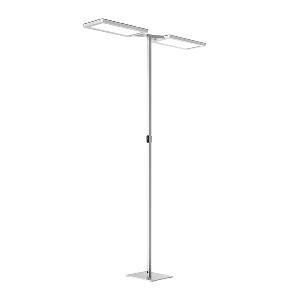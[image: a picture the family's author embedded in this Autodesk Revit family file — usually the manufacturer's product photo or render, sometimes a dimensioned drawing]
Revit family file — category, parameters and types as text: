
# Revit family: yara_doublet_-_yts_2_15000_vtl_r_sr_cee_s0_c_114268000-00808493_cb8c
name_source: partatom
category: Lighting Fixtures
units: mm (PartAtom-declared; Revit-internal decimal feet)

## family parameters
Cut with Voids When Loaded = No
Host = Face
Light Source = No
Part Type = Normal
Room Calculation Point = No
Round Connector Dimension = Use Diameter
Shared = No

## types (1)
- YARA.doubleT - YTS 2/15000/VTL/R/SR/CEE/S0/C (1 x LED, 15000 lm, VTL)
    Apparent Load = 214 VA
    Approval mark = CE
    CIE Flux Codes = 58 87 97 13 100
    Color Rendering = 80-89
    Color Temperature = VTL
    Control Gear = Electronic ballast
    Default Elevation = 1800 mm
    Description = YTS 2/15000/VTL/R/SR/CEE/S0/R|Free-standing luminaire|light source: LED Daylight 2700-6500 K  Energy efficiency category A/A+/A++|work equipment: Electronic ballast DALI|connected load: 220-240 V, 50/60 Hz|Power consumption: approx. 210 W|power factor: approx. 0,966|luminous flux: 30000 lm|luminous efficacy: 142 lm/W|light distribution: Direct/indirect|direct ratio: approx. 13 %|color rendering index (CRI): >= 80|chromaticity tolerance:  3 SDCM|technology: Presence and daylight sensor control (PIR)|operation: Wireless switch|luminaire body|material: Aluminium/plastic|surface: Powder coatet|colour: Silver metallic|lamp cover: Acrylic (PMMA), Satine, Structured|tubular section|material: Steel tube|surface: Powder-coated|Form: Tubular section upright|colour of tubular section: Silver metallic|luminaire base|Form: Rectangular flat|weight (net): approx. 24.0 kg|mains lead: 3.00 m Mains plug CEE 7/VII|Fastening: Floor standing base|glare control: Conical prismatic screen|luminance(L65): <= 2700 cd/m|unified glare rating(4H 8H): <=  16|special features: App control, Asymmetric radiation, Biodynamic light VTL, Direct and indirect lighting component with edge light and light guidetechnology for a homogeneous light exit, Flicker-free, Magnetic control panel, freely positionable, PIR movement and daylight sensor, TALK Bluetooth|Approval mark: VDE - ENEC|
    Frequency = 50 Hz, 60 Hz
    Height = 24 mm  [stored 0.0787402 ft]
    Lamp = 1 x LED
    Lamp Light Flux = 15000 lm
    Lamp count = 1
    Length = 690 mm
    Luminous efficacy = 140 lm/W
    Manufacturer = Waldmann
    ModVariant = No
    Model = 114268000-00808493
    Mounting Place = Floor
    Mounting Type = Freestanding
    Number of Poles = 1
    OnlyDefault = Yes
    Power Factor = 1
    Product Name = YARA.doubleT - YTS 2/15000/VTL/R/SR/CEE/S0/C
    Product group = Free standing luminaire
    ProductGroupID = 13
    Protection Class = Protection class I
    Protection Degree = IP 20
    RLX_Detail_Level = 1
    RlxData = <blob elided: 63513 chars, md5=cb42fa3b>
    Socket = socket
    Standby Power = 0 W
    System Light Flux = 30000 lm
    System Power = 214 W
    Type Comments = Product without accessories
    Type Image = yts-r-sr-r.jpg
    URL = http://relux.com
    VarID = ---
    Voltage = 230 V
    Voltage Range = 220-240 V
    Weight = 0.00 kg
    Width = 358 mm

note: [stored X ft] marks values corroborated as IEEE doubles in the binary element streams (Revit-internal decimal feet)

## geometry (parser evidence)
native form markers: Blend x4, Sweep x20
no freeform markers — native parametric forms only
